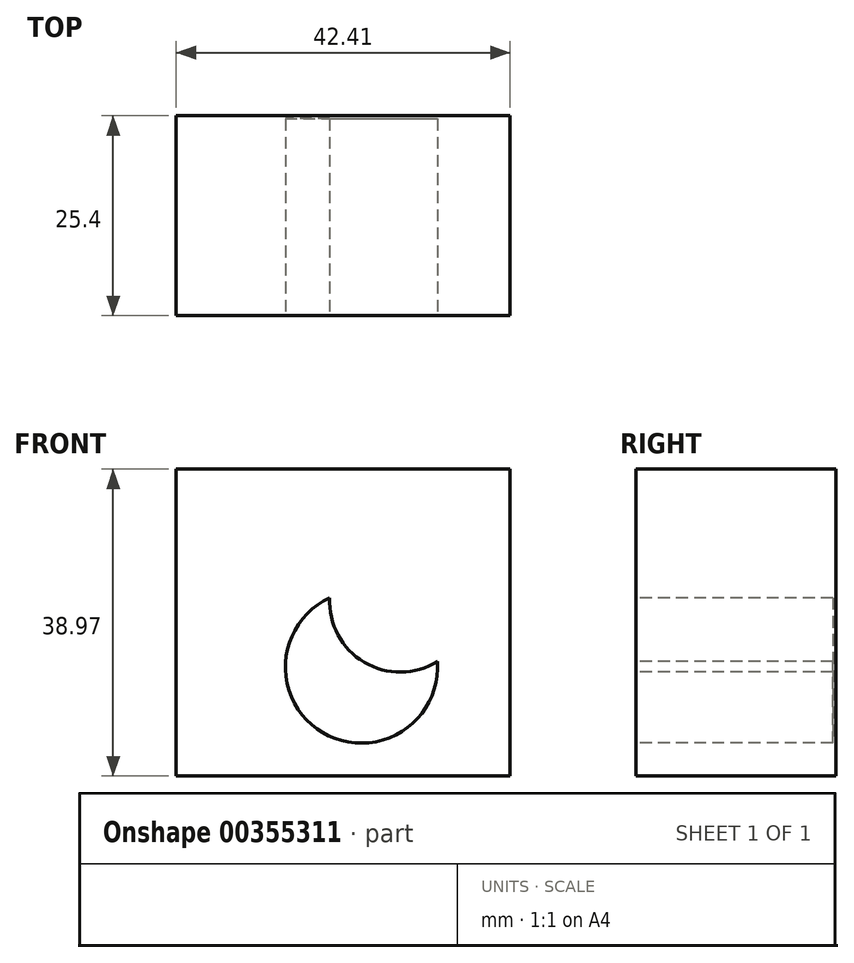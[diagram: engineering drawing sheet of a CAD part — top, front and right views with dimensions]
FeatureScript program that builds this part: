
annotation { "Feature Type Name" : "Feature", "Feature Type Description" : "" }
export const myFeature = defineFeature(function(context is Context, id is Id, definition is map)
    precondition{}
    {
        {
            var Q0;
            Q0=qCreatedBy(makeId("Front.planeOp"),FACE);
            var sketch = newSketch(context, id + "F0", { "sketchPlane" : qUnion([Q0])});
            skLineSegment(sketch, "E0.bottom", {"start": v(0, 0) * mm, "end": v(42.41, 0) * mm});
            skLineSegment(sketch, "E0.top", {"start": v(0, 38.97) * mm, "end": v(42.41, 38.97) * mm});
            skLineSegment(sketch, "E0.left", {"start": v(0, 0) * mm, "end": v(0, 38.97) * mm});
            skLineSegment(sketch, "E0.right", {"start": v(42.41, 0) * mm, "end": v(42.41, 38.97) * mm});
            skSolve(sketch);
        }
        {
            var Q0;
            Q0 = qSketchRegion(id + "F0", true);
            extrude(context, id + "F1", {"entities" : qUnion([Q0]), "depth" : 25.4 * mm});
        }
        {
            var Q0;
            Q0=makeQuery(id+"F1.opExtrude","CAP_FACE",FACE,{"disambiguationData":[OSD([sQuery(id+"F0.wireOp",EDGE,"E0.bottom"),sQuery(id+"F0.wireOp",EDGE,"E0.top"),sQuery(id+"F0.wireOp",EDGE,"E0.left"),sQuery(id+"F0.wireOp",EDGE,"E0.right")])],"isStart":false});
            var sketch = newSketch(context, id + "F2", { "sketchPlane" : qUnion([Q0])});
            skCircle(sketch, "E1", {"center": v(14.66, 26.05) * mm, "radius": 6.5 * mm});
            skSolve(sketch);
        }
        {
            var Q0;
            Q0=sQuery(id+"F2.wireOp",EDGE,"E1");
            extrude(context, id + "F3", {"bodyType" : ToolBodyType.SURFACE, "surfaceEntities" : qUnion([Q0]), "endBound" : BoundingType.SYMMETRIC, "depth" : 12 * mm});
        }
        {
            var Q0;
            Q0=makeQuery(id+"F1.opExtrude","CAP_FACE",FACE,{"disambiguationData":[OSD([sQuery(id+"F0.wireOp",EDGE,"E0.bottom"),sQuery(id+"F0.wireOp",EDGE,"E0.top"),sQuery(id+"F0.wireOp",EDGE,"E0.left"),sQuery(id+"F0.wireOp",EDGE,"E0.right")])],"isStart":false});
            var sketch = newSketch(context, id + "F4", { "sketchPlane" : qUnion([Q0])});
            skCircle(sketch, "E2", {"center": v(23.53, 13.83) * mm, "radius": 9.67 * mm});
            skCircle(sketch, "E3", {"center": v(28.46, 22.15) * mm, "radius": 8.97 * mm});
            skSolve(sketch);
        }
        {
            var Q0;
            {var subQ0=sQuery(id+"F4.wireOp",EDGE,"E3");var subQ1=sQuery(id+"F4.wireOp",EDGE,"E2");var subQ2=makeQuery(id+"F4.imprint","INTERSECT",VERTEX,{"disambiguationData":[OD(0.0)],"derivedFrom":[subQ1,subQ0]});Q0=makeQuery(id+"F4.imprint","IMPRINT",FACE,{"disambiguationData":[TD([[makeQuery(id+"F4.imprint","IMPRINT",EDGE,{"disambiguationData":[TD([[subQ2,-1.0]])],"derivedFrom":subQ1}),1.0]])]});}
            extrude(context, id + "F5", {"entities" : qUnion([Q0]), "operationType" : NewBodyOperationType.REMOVE, "oppositeDirection" : true, "depth" : 25 * mm});
        }
    });
